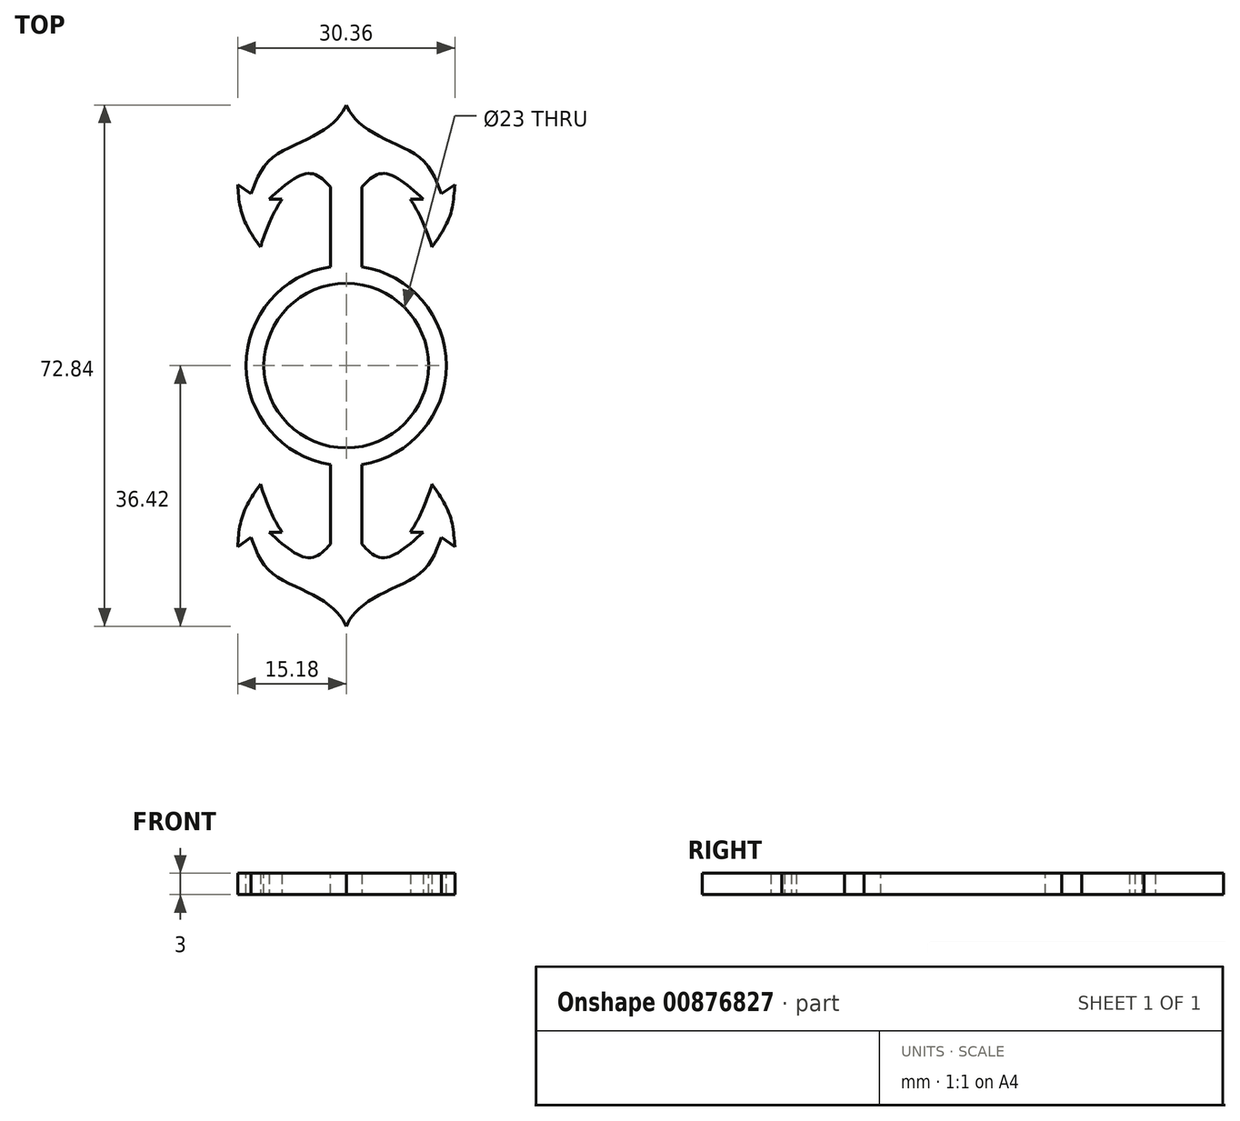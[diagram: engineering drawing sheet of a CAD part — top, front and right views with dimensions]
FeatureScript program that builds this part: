
annotation { "Feature Type Name" : "Feature", "Feature Type Description" : "" }
export const myFeature = defineFeature(function(context is Context, id is Id, definition is map)
    precondition{}
    {
        {
            var Q0;
            Q0=qCreatedBy(makeId("Top.planeOp"),FACE);
            var sketch = newSketch(context, id + "F0", { "sketchPlane" : qUnion([Q0])});
            skCircle(sketch, "E0", {"center": v(0, 0) * mm, "radius": 10 * mm});
            skSolve(sketch);
        }
        {
            var Q0;
            Q0=qCreatedBy(makeId("Top.planeOp"),FACE);
            var sketch = newSketch(context, id + "F1", { "sketchPlane" : qUnion([Q0])});
            skLineSegment(sketch, "E1", {"start": v(3.6, 24.28) * mm, "end": v(3.6, 20.2) * mm});
            skLineSegment(sketch, "E2", {"start": v(3.6, 20.2) * mm, "end": v(16.25, 20.2) * mm});
            skLineSegment(sketch, "E3", {"start": v(16.25, 20.2) * mm, "end": v(13.66, 15.85) * mm});
            skLineSegment(sketch, "E4", {"start": v(13.66, 15.85) * mm, "end": v(3.67, 15.85) * mm});
            skLineSegment(sketch, "E5", {"start": v(3.67, 15.85) * mm, "end": v(3.67, -11.08) * mm});
            skFitSpline(sketch, "E6", {"points": [v(3.67, -11.08) * mm, v(8.7, -14.26) * mm, v(17.95, -8.27) * mm], "startDerivative": vector(10.83, -12.27) * mm, "endDerivative": vector(17.41, 15.81) * mm});
            skLineSegment(sketch, "E7", {"start": v(17.95, -8.27) * mm, "end": v(14.96, -8.27) * mm});
            skFitSpline(sketch, "E8", {"points": [v(14.96, -8.27) * mm, v(17.4, -3.92) * mm, v(19.99, 2.88) * mm], "startDerivative": vector(5.56, 8.96) * mm, "endDerivative": vector(4.54, 13.2) * mm});
            skFitSpline(sketch, "E9", {"points": [v(19.99, 2.88) * mm, v(24.07, -4.2) * mm, v(25.3, -11.67) * mm], "startDerivative": vector(9.41, -13.54) * mm, "endDerivative": vector(1.14, -15.57) * mm});
            skLineSegment(sketch, "E10", {"start": v(25.3, -11.67) * mm, "end": v(22.17, -9.5) * mm});
            skPoint(sketch, "E11.4.internal.snap0", {"position": v(0, -30.63) * mm});
            skFitSpline(sketch, "E11", {"points": [v(22.17, -9.5) * mm, v(18.09, -17.11) * mm, v(9.52, -22) * mm, v(2.45, -26.63) * mm, v(0, -30.2) * mm], "startDerivative": vector(-11.25, -30.6) * mm, "endDerivative": vector(-6.4, -14.97) * mm});
            skArc(sketch, "E12", {"start": v(3.6, 24.28) * mm, "mid": v(7.05, 32.48) * mm, "end": v(0, 37.9) * mm});
            skArc(sketch, "E13.MirrorCS", {"start": v(-3.6, 24.28) * mm, "mid": v(-7.05, 32.48) * mm, "end": v(0, 37.9) * mm});
            skLineSegment(sketch, "E14.MirrorCS", {"start": v(-3.6, 24.28) * mm, "end": v(-3.6, 20.2) * mm});
            skLineSegment(sketch, "E15.MirrorCS", {"start": v(-3.6, 20.2) * mm, "end": v(-16.25, 20.2) * mm});
            skLineSegment(sketch, "E16.MirrorCS", {"start": v(-16.25, 20.2) * mm, "end": v(-13.66, 15.85) * mm});
            skLineSegment(sketch, "E17.MirrorCS", {"start": v(-13.66, 15.85) * mm, "end": v(-3.67, 15.85) * mm});
            skLineSegment(sketch, "E18.MirrorCS", {"start": v(-3.67, 15.85) * mm, "end": v(-3.67, -11.08) * mm});
            skFitSpline(sketch, "E19.MirrorCS", {"points": [v(-3.67, -11.08) * mm, v(-8.7, -14.26) * mm, v(-17.95, -8.27) * mm], "startDerivative": vector(-10.83, -12.27) * mm, "endDerivative": vector(-17.41, 15.81) * mm});
            skFitSpline(sketch, "E20.MirrorCS", {"points": [v(-14.96, -8.27) * mm, v(-17.4, -3.92) * mm, v(-19.99, 2.88) * mm], "startDerivative": vector(-5.56, 8.96) * mm, "endDerivative": vector(-4.54, 13.2) * mm});
            skFitSpline(sketch, "E21.MirrorCS", {"points": [v(-19.99, 2.88) * mm, v(-24.07, -4.2) * mm, v(-25.3, -11.67) * mm], "startDerivative": vector(-9.41, -13.54) * mm, "endDerivative": vector(-1.14, -15.57) * mm});
            skLineSegment(sketch, "E22.MirrorCS", {"start": v(-17.95, -8.27) * mm, "end": v(-14.96, -8.27) * mm});
            skLineSegment(sketch, "E23.MirrorCS", {"start": v(-25.3, -11.67) * mm, "end": v(-22.17, -9.5) * mm});
            skFitSpline(sketch, "E24.MirrorCS", {"points": [v(-22.17, -9.5) * mm, v(-18.09, -17.11) * mm, v(-9.52, -22) * mm, v(-2.45, -26.63) * mm, v(0, -30.2) * mm], "startDerivative": vector(11.25, -30.6) * mm, "endDerivative": vector(6.4, -14.97) * mm});
            skCircle(sketch, "E25", {"center": v(0, 30.62) * mm, "radius": 3.57 * mm});
            skSolve(sketch);
        }
        {
            var Q0;
            Q0=makeQuery(id+"F1.imprint","IMPRINT",FACE,{"disambiguationData":[TD([[makeQuery(id+"F1.imprint","IMPRINT",EDGE,{"derivedFrom":sQuery(id+"F1.wireOp",EDGE,"E1")}),-1.0]])]});
            extrude(context, id + "F2", {"entities" : qUnion([Q0]), "depth" : 5 * mm, "offsetDistance" : 25 * mm});
        }
        {
            var Q0;
            Q0=makeQuery(id+"F2.opExtrude","SWEPT_BODY",BODY,{"disambiguationData":[OSD([sQuery(id+"F1.wireOp",EDGE,"E1"),sQuery(id+"F1.wireOp",EDGE,"E2"),sQuery(id+"F1.wireOp",EDGE,"E3"),sQuery(id+"F1.wireOp",EDGE,"E4"),sQuery(id+"F1.wireOp",EDGE,"E5"),sQuery(id+"F1.wireOp",EDGE,"E6"),sQuery(id+"F1.wireOp",EDGE,"E7"),sQuery(id+"F1.wireOp",EDGE,"E8"),sQuery(id+"F1.wireOp",EDGE,"E9"),sQuery(id+"F1.wireOp",EDGE,"E10"),sQuery(id+"F1.wireOp",EDGE,"E11"),sQuery(id+"F1.wireOp",EDGE,"E12"),sQuery(id+"F1.wireOp",EDGE,"E13.MirrorCS"),sQuery(id+"F1.wireOp",EDGE,"E14.MirrorCS"),sQuery(id+"F1.wireOp",EDGE,"E15.MirrorCS"),sQuery(id+"F1.wireOp",EDGE,"E16.MirrorCS"),sQuery(id+"F1.wireOp",EDGE,"E17.MirrorCS"),sQuery(id+"F1.wireOp",EDGE,"E18.MirrorCS"),sQuery(id+"F1.wireOp",EDGE,"E19.MirrorCS"),sQuery(id+"F1.wireOp",EDGE,"E20.MirrorCS"),sQuery(id+"F1.wireOp",EDGE,"E21.MirrorCS"),sQuery(id+"F1.wireOp",EDGE,"E22.MirrorCS"),sQuery(id+"F1.wireOp",EDGE,"E23.MirrorCS"),sQuery(id+"F1.wireOp",EDGE,"E24.MirrorCS"),sQuery(id+"F1.wireOp",EDGE,"E25")])]});
            var Q1;
            Q1=sQuery(id+"F0.wireOp",VERTEX,"E0.center");
            transform(context, id + "F3", {"entities" : qUnion([Q0]), "transformType" : TransformType.TRANSLATION_3D, "dx" : 0 * mm, "dy" : -30.5 * mm, "dz" : 0 * mm, "makeCopy" : false});
        }
        {
            var Q0;
            Q0=makeQuery(id+"F2.opExtrude","SWEPT_BODY",BODY,{"disambiguationData":[OSD([sQuery(id+"F1.wireOp",EDGE,"E1"),sQuery(id+"F1.wireOp",EDGE,"E2"),sQuery(id+"F1.wireOp",EDGE,"E3"),sQuery(id+"F1.wireOp",EDGE,"E4"),sQuery(id+"F1.wireOp",EDGE,"E5"),sQuery(id+"F1.wireOp",EDGE,"E6"),sQuery(id+"F1.wireOp",EDGE,"E7"),sQuery(id+"F1.wireOp",EDGE,"E8"),sQuery(id+"F1.wireOp",EDGE,"E9"),sQuery(id+"F1.wireOp",EDGE,"E10"),sQuery(id+"F1.wireOp",EDGE,"E11"),sQuery(id+"F1.wireOp",EDGE,"E12"),sQuery(id+"F1.wireOp",EDGE,"E13.MirrorCS"),sQuery(id+"F1.wireOp",EDGE,"E14.MirrorCS"),sQuery(id+"F1.wireOp",EDGE,"E15.MirrorCS"),sQuery(id+"F1.wireOp",EDGE,"E16.MirrorCS"),sQuery(id+"F1.wireOp",EDGE,"E17.MirrorCS"),sQuery(id+"F1.wireOp",EDGE,"E18.MirrorCS"),sQuery(id+"F1.wireOp",EDGE,"E19.MirrorCS"),sQuery(id+"F1.wireOp",EDGE,"E20.MirrorCS"),sQuery(id+"F1.wireOp",EDGE,"E21.MirrorCS"),sQuery(id+"F1.wireOp",EDGE,"E22.MirrorCS"),sQuery(id+"F1.wireOp",EDGE,"E23.MirrorCS"),sQuery(id+"F1.wireOp",EDGE,"E24.MirrorCS"),sQuery(id+"F1.wireOp",EDGE,"E25")])]});
            var Q1;
            Q1=sQuery(id+"F0.wireOp",VERTEX,"E0.center");
            transform(context, id + "F4", {"entities" : qUnion([Q0]), "transformType" : TransformType.SCALE_UNIFORMLY, "scale" : 1.5, "scalePoint" : qUnion([Q1]), "makeCopy" : false});
        }
        {
            var Q0;
            Q0=makeQuery(id+"F2.opExtrude","CAP_FACE",FACE,{"disambiguationData":[OSD([sQuery(id+"F1.wireOp",EDGE,"E1"),sQuery(id+"F1.wireOp",EDGE,"E2"),sQuery(id+"F1.wireOp",EDGE,"E3"),sQuery(id+"F1.wireOp",EDGE,"E4"),sQuery(id+"F1.wireOp",EDGE,"E5"),sQuery(id+"F1.wireOp",EDGE,"E6"),sQuery(id+"F1.wireOp",EDGE,"E7"),sQuery(id+"F1.wireOp",EDGE,"E8"),sQuery(id+"F1.wireOp",EDGE,"E9"),sQuery(id+"F1.wireOp",EDGE,"E10"),sQuery(id+"F1.wireOp",EDGE,"E11"),sQuery(id+"F1.wireOp",EDGE,"E12"),sQuery(id+"F1.wireOp",EDGE,"E13.MirrorCS"),sQuery(id+"F1.wireOp",EDGE,"E14.MirrorCS"),sQuery(id+"F1.wireOp",EDGE,"E15.MirrorCS"),sQuery(id+"F1.wireOp",EDGE,"E16.MirrorCS"),sQuery(id+"F1.wireOp",EDGE,"E17.MirrorCS"),sQuery(id+"F1.wireOp",EDGE,"E18.MirrorCS"),sQuery(id+"F1.wireOp",EDGE,"E19.MirrorCS"),sQuery(id+"F1.wireOp",EDGE,"E20.MirrorCS"),sQuery(id+"F1.wireOp",EDGE,"E21.MirrorCS"),sQuery(id+"F1.wireOp",EDGE,"E22.MirrorCS"),sQuery(id+"F1.wireOp",EDGE,"E23.MirrorCS"),sQuery(id+"F1.wireOp",EDGE,"E24.MirrorCS"),sQuery(id+"F1.wireOp",EDGE,"E25")])],"isStart":false});
            var sketch = newSketch(context, id + "F5", { "sketchPlane" : qUnion([Q0])});
            skSolve(sketch);
        }
        {
            var Q0;
            Q0=makeQuery(id+"F2.opExtrude","SWEPT_BODY",BODY,{"disambiguationData":[OSD([sQuery(id+"F1.wireOp",EDGE,"E1"),sQuery(id+"F1.wireOp",EDGE,"E2"),sQuery(id+"F1.wireOp",EDGE,"E3"),sQuery(id+"F1.wireOp",EDGE,"E4"),sQuery(id+"F1.wireOp",EDGE,"E5"),sQuery(id+"F1.wireOp",EDGE,"E6"),sQuery(id+"F1.wireOp",EDGE,"E7"),sQuery(id+"F1.wireOp",EDGE,"E8"),sQuery(id+"F1.wireOp",EDGE,"E9"),sQuery(id+"F1.wireOp",EDGE,"E10"),sQuery(id+"F1.wireOp",EDGE,"E11"),sQuery(id+"F1.wireOp",EDGE,"E12"),sQuery(id+"F1.wireOp",EDGE,"E13.MirrorCS"),sQuery(id+"F1.wireOp",EDGE,"E14.MirrorCS"),sQuery(id+"F1.wireOp",EDGE,"E15.MirrorCS"),sQuery(id+"F1.wireOp",EDGE,"E16.MirrorCS"),sQuery(id+"F1.wireOp",EDGE,"E17.MirrorCS"),sQuery(id+"F1.wireOp",EDGE,"E18.MirrorCS"),sQuery(id+"F1.wireOp",EDGE,"E19.MirrorCS"),sQuery(id+"F1.wireOp",EDGE,"E20.MirrorCS"),sQuery(id+"F1.wireOp",EDGE,"E21.MirrorCS"),sQuery(id+"F1.wireOp",EDGE,"E22.MirrorCS"),sQuery(id+"F1.wireOp",EDGE,"E23.MirrorCS"),sQuery(id+"F1.wireOp",EDGE,"E24.MirrorCS"),sQuery(id+"F1.wireOp",EDGE,"E25")])]});
            var Q1;
            Q1=sQuery(id+"F0.wireOp",EDGE,"E0");
            circularPattern(context, id + "F6", {"entities" : qUnion([Q0]), "axis" : qUnion([Q1]), "angle" : 360 * degree, "instanceCount" : 2, "equalSpace" : true});
        }
        {
            var Q0;
            Q0=makeQuery(id+"F5.imprint","IMPRINT",FACE,{"disambiguationData":[TD([[makeQuery(id+"F5.imprint","IMPRINT",EDGE,{"derivedFrom":makeQuery(id+"F2.opExtrude","CAP_EDGE",EDGE,{"disambiguationData":[OSD([sQuery(id+"F1.wireOp",EDGE,"E1")])],"isStart":false})}),-1.0]])]});
            var sketch = newSketch(context, id + "F7", { "sketchPlane" : qUnion([Q0])});
            skCircle(sketch, "E26", {"center": v(0, 0) * mm, "radius": 15 * mm});
            skSolve(sketch);
        }
        {
            var Q0;
            {var subQ5=makeQuery(id+"F5.imprint","IMPRINT",EDGE,{"derivedFrom":makeQuery(id+"F2.opExtrude","CAP_EDGE",EDGE,{"disambiguationData":[OSD([sQuery(id+"F1.wireOp",EDGE,"E12"),sQuery(id+"F1.wireOp",EDGE,"E13.MirrorCS")])],"isStart":false})});Q0=makeQuery(id+"F7.imprint","IMPRINT",FACE,{"disambiguationData":[TD([[makeQuery(id+"F7.imprint","IMPRINT",EDGE,{"derivedFrom":subQ5}),-1.0]])]});}
            var Q1;
            Q1=sQuery(id+"F7.wireOp",EDGE,"E26");
            extrude(context, id + "F8", {"entities" : qUnion([Q0]), "operationType" : NewBodyOperationType.ADD, "surfaceEntities" : qUnion([Q1]), "oppositeDirection" : true, "depth" : 7.5 * mm, "offsetDistance" : 25 * mm});
        }
        {
            var Q0;
            {var subQ0=sQuery(id+"F1.wireOp",EDGE,"E14.MirrorCS");var subQ1=sQuery(id+"F1.wireOp",EDGE,"E13.MirrorCS");var subQ2=sQuery(id+"F1.wireOp",EDGE,"E12");var subQ3=sQuery(id+"F1.wireOp",EDGE,"E1");var subQ4=makeQuery(id+"F2.opExtrude","CAP_FACE",FACE,{"disambiguationData":[OSD([subQ3,sQuery(id+"F1.wireOp",EDGE,"E2"),sQuery(id+"F1.wireOp",EDGE,"E3"),sQuery(id+"F1.wireOp",EDGE,"E4"),sQuery(id+"F1.wireOp",EDGE,"E5"),sQuery(id+"F1.wireOp",EDGE,"E6"),sQuery(id+"F1.wireOp",EDGE,"E7"),sQuery(id+"F1.wireOp",EDGE,"E8"),sQuery(id+"F1.wireOp",EDGE,"E9"),sQuery(id+"F1.wireOp",EDGE,"E10"),sQuery(id+"F1.wireOp",EDGE,"E11"),subQ2,subQ1,subQ0,sQuery(id+"F1.wireOp",EDGE,"E15.MirrorCS"),sQuery(id+"F1.wireOp",EDGE,"E16.MirrorCS"),sQuery(id+"F1.wireOp",EDGE,"E17.MirrorCS"),sQuery(id+"F1.wireOp",EDGE,"E18.MirrorCS"),sQuery(id+"F1.wireOp",EDGE,"E19.MirrorCS"),sQuery(id+"F1.wireOp",EDGE,"E20.MirrorCS"),sQuery(id+"F1.wireOp",EDGE,"E21.MirrorCS"),sQuery(id+"F1.wireOp",EDGE,"E22.MirrorCS"),sQuery(id+"F1.wireOp",EDGE,"E23.MirrorCS"),sQuery(id+"F1.wireOp",EDGE,"E24.MirrorCS"),sQuery(id+"F1.wireOp",EDGE,"E25")])],"isStart":false});Q0=makeQuery(id+"F8.boolean.opBoolean","MERGE",FACE,{"derivedFrom":[subQ4,makeQuery(id+"F6.opPattern","COPY",FACE,{"derivedFrom":subQ4,"instanceName":"1"}),makeQuery(id+"F8.opExtrude","CAP_FACE",FACE,{"disambiguationData":[OSD([subQ3,subQ2,subQ1,subQ0,sQuery(id+"F7.wireOp",EDGE,"E26")])],"isStart":true})]});}
            var sketch = newSketch(context, id + "F9", { "sketchPlane" : qUnion([Q0])});
            skCircle(sketch, "E27", {"center": v(0, 0) * mm, "radius": 11.5 * mm});
            skSolve(sketch);
        }
        {
            var Q0;
            Q0 = qSketchRegion(id + "F9", true);
            extrude(context, id + "F10", {"entities" : qUnion([Q0]), "operationType" : NewBodyOperationType.REMOVE, "oppositeDirection" : true, "depth" : 25 * mm, "offsetDistance" : 25 * mm});
        }
        {
            var Q0;
            Q0=makeQuery(id+"F2.opExtrude","SWEPT_BODY",BODY,{"disambiguationData":[OSD([sQuery(id+"F1.wireOp",EDGE,"E1"),sQuery(id+"F1.wireOp",EDGE,"E2"),sQuery(id+"F1.wireOp",EDGE,"E3"),sQuery(id+"F1.wireOp",EDGE,"E4"),sQuery(id+"F1.wireOp",EDGE,"E5"),sQuery(id+"F1.wireOp",EDGE,"E6"),sQuery(id+"F1.wireOp",EDGE,"E7"),sQuery(id+"F1.wireOp",EDGE,"E8"),sQuery(id+"F1.wireOp",EDGE,"E9"),sQuery(id+"F1.wireOp",EDGE,"E10"),sQuery(id+"F1.wireOp",EDGE,"E11"),sQuery(id+"F1.wireOp",EDGE,"E12"),sQuery(id+"F1.wireOp",EDGE,"E13.MirrorCS"),sQuery(id+"F1.wireOp",EDGE,"E14.MirrorCS"),sQuery(id+"F1.wireOp",EDGE,"E15.MirrorCS"),sQuery(id+"F1.wireOp",EDGE,"E16.MirrorCS"),sQuery(id+"F1.wireOp",EDGE,"E17.MirrorCS"),sQuery(id+"F1.wireOp",EDGE,"E18.MirrorCS"),sQuery(id+"F1.wireOp",EDGE,"E19.MirrorCS"),sQuery(id+"F1.wireOp",EDGE,"E20.MirrorCS"),sQuery(id+"F1.wireOp",EDGE,"E21.MirrorCS"),sQuery(id+"F1.wireOp",EDGE,"E22.MirrorCS"),sQuery(id+"F1.wireOp",EDGE,"E23.MirrorCS"),sQuery(id+"F1.wireOp",EDGE,"E24.MirrorCS"),sQuery(id+"F1.wireOp",EDGE,"E25")])]});
            var Q1;
            Q1=sQuery(id+"F0.wireOp",VERTEX,"E0.center");
            var Q2;
            Q2=sQuery(id+"F0.wireOp",VERTEX,"E0.center");
            transform(context, id + "F11", {"entities" : qUnion([Q0]), "transformType" : TransformType.SCALE_UNIFORMLY, "scale" : 0.4, "scalePoint" : qUnion([Q2]), "makeCopy" : false});
        }
        {
            var Q0;
            {var subQ0=sQuery(id+"F1.wireOp",EDGE,"E14.MirrorCS");var subQ1=sQuery(id+"F1.wireOp",EDGE,"E13.MirrorCS");var subQ2=sQuery(id+"F1.wireOp",EDGE,"E12");var subQ3=sQuery(id+"F1.wireOp",EDGE,"E1");var subQ4=makeQuery(id+"F2.opExtrude","CAP_FACE",FACE,{"disambiguationData":[OSD([subQ3,sQuery(id+"F1.wireOp",EDGE,"E2"),sQuery(id+"F1.wireOp",EDGE,"E3"),sQuery(id+"F1.wireOp",EDGE,"E4"),sQuery(id+"F1.wireOp",EDGE,"E5"),sQuery(id+"F1.wireOp",EDGE,"E6"),sQuery(id+"F1.wireOp",EDGE,"E7"),sQuery(id+"F1.wireOp",EDGE,"E8"),sQuery(id+"F1.wireOp",EDGE,"E9"),sQuery(id+"F1.wireOp",EDGE,"E10"),sQuery(id+"F1.wireOp",EDGE,"E11"),subQ2,subQ1,subQ0,sQuery(id+"F1.wireOp",EDGE,"E15.MirrorCS"),sQuery(id+"F1.wireOp",EDGE,"E16.MirrorCS"),sQuery(id+"F1.wireOp",EDGE,"E17.MirrorCS"),sQuery(id+"F1.wireOp",EDGE,"E18.MirrorCS"),sQuery(id+"F1.wireOp",EDGE,"E19.MirrorCS"),sQuery(id+"F1.wireOp",EDGE,"E20.MirrorCS"),sQuery(id+"F1.wireOp",EDGE,"E21.MirrorCS"),sQuery(id+"F1.wireOp",EDGE,"E22.MirrorCS"),sQuery(id+"F1.wireOp",EDGE,"E23.MirrorCS"),sQuery(id+"F1.wireOp",EDGE,"E24.MirrorCS"),sQuery(id+"F1.wireOp",EDGE,"E25")])],"isStart":false});Q0=makeQuery(id+"F8.boolean.opBoolean","MERGE",FACE,{"derivedFrom":[subQ4,makeQuery(id+"F6.opPattern","COPY",FACE,{"derivedFrom":subQ4,"instanceName":"1"}),makeQuery(id+"F8.opExtrude","CAP_FACE",FACE,{"disambiguationData":[OSD([subQ3,subQ2,subQ1,subQ0,sQuery(id+"F7.wireOp",EDGE,"E26")])],"isStart":true})]});}
            var sketch = newSketch(context, id + "F12", { "sketchPlane" : qUnion([Q0])});
            skCircle(sketch, "E28", {"center": v(0, 0) * mm, "radius": 14 * mm});
            skSolve(sketch);
        }
        {
            var Q0;
            Q0 = qSketchRegion(id + "F12", true);
            extrude(context, id + "F13", {"entities" : qUnion([Q0]), "operationType" : NewBodyOperationType.ADD, "oppositeDirection" : true, "depth" : 3 * mm, "offsetDistance" : 25 * mm});
        }
        {
            var Q0;
            {var subQ0=sQuery(id+"F1.wireOp",EDGE,"E14.MirrorCS");var subQ1=sQuery(id+"F1.wireOp",EDGE,"E13.MirrorCS");var subQ2=sQuery(id+"F1.wireOp",EDGE,"E12");var subQ3=sQuery(id+"F1.wireOp",EDGE,"E1");var subQ4=makeQuery(id+"F2.opExtrude","CAP_FACE",FACE,{"disambiguationData":[OSD([subQ3,sQuery(id+"F1.wireOp",EDGE,"E2"),sQuery(id+"F1.wireOp",EDGE,"E3"),sQuery(id+"F1.wireOp",EDGE,"E4"),sQuery(id+"F1.wireOp",EDGE,"E5"),sQuery(id+"F1.wireOp",EDGE,"E6"),sQuery(id+"F1.wireOp",EDGE,"E7"),sQuery(id+"F1.wireOp",EDGE,"E8"),sQuery(id+"F1.wireOp",EDGE,"E9"),sQuery(id+"F1.wireOp",EDGE,"E10"),sQuery(id+"F1.wireOp",EDGE,"E11"),subQ2,subQ1,subQ0,sQuery(id+"F1.wireOp",EDGE,"E15.MirrorCS"),sQuery(id+"F1.wireOp",EDGE,"E16.MirrorCS"),sQuery(id+"F1.wireOp",EDGE,"E17.MirrorCS"),sQuery(id+"F1.wireOp",EDGE,"E18.MirrorCS"),sQuery(id+"F1.wireOp",EDGE,"E19.MirrorCS"),sQuery(id+"F1.wireOp",EDGE,"E20.MirrorCS"),sQuery(id+"F1.wireOp",EDGE,"E21.MirrorCS"),sQuery(id+"F1.wireOp",EDGE,"E22.MirrorCS"),sQuery(id+"F1.wireOp",EDGE,"E23.MirrorCS"),sQuery(id+"F1.wireOp",EDGE,"E24.MirrorCS"),sQuery(id+"F1.wireOp",EDGE,"E25")])],"isStart":false});Q0=makeQuery(id+"F13.boolean.opBoolean","MERGE",FACE,{"derivedFrom":[makeQuery(id+"F8.boolean.opBoolean","MERGE",FACE,{"derivedFrom":[subQ4,makeQuery(id+"F6.opPattern","COPY",FACE,{"derivedFrom":subQ4,"instanceName":"1"}),makeQuery(id+"F8.opExtrude","CAP_FACE",FACE,{"disambiguationData":[OSD([subQ3,subQ2,subQ1,subQ0,sQuery(id+"F7.wireOp",EDGE,"E26")])],"isStart":true})]}),makeQuery(id+"F13.opExtrude","CAP_FACE",FACE,{"disambiguationData":[OSD([sQuery(id+"F12.wireOp",EDGE,"E28")])],"isStart":true})]});}
            var sketch = newSketch(context, id + "F14", { "sketchPlane" : qUnion([Q0])});
            skCircle(sketch, "E29", {"center": v(0, 0) * mm, "radius": 11.5 * mm});
            skSolve(sketch);
        }
        {
            var Q0;
            Q0 = qSketchRegion(id + "F14", true);
            extrude(context, id + "F15", {"entities" : qUnion([Q0]), "operationType" : NewBodyOperationType.REMOVE, "oppositeDirection" : true, "depth" : 25 * mm, "offsetDistance" : 25 * mm});
        }
    });
